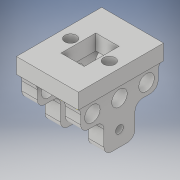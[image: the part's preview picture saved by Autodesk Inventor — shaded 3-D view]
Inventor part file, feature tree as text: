
AUTODESK INVENTOR PART (.ipt)
format: ipt  version: 2019 (Build 230136000, 136)  size: 258,048 bytes
history: native  units: mm
features: extrude x8, sketch x8, fillet x4, hole x1
ambient origin geometry x8: Origin, YZ Plane, XZ Plane, XY Plane, X Axis, Y Axis, Z Axis, Center Point
bodies: Solid1 (feature_tree)
feature tree (21):
  extrude  "Extrusion1"  Depth=80.0mm
  extrude  "Extrusion2"  Depth=30.0mm
  hole  "Hole1"  [1 undecoded]
  extrude  "Extrusion3"  Depth=20.0mm
  fillet  "Fillet1"  Radius=2.0mm
  fillet  "Fillet3"  Radius=30.0mm
  extrude  "Extrusion4"  Depth=15.0mm
  sketch  "Sketch6"  dims[d20=15.0mm d21=25.0mm]
  extrude  "Extrusion6"  Depth=25.0mm
  extrude  "Extrusion7"  Depth=15.0mm TaperAngle=0.0deg
  extrude  "Extrusion8"  Depth=10.0mm
  extrude  "Extrusion9"  Depth=45.0mm
  fillet  "Fillet7"  Radius=30.0mm
  fillet  "Fillet8"  Radius=20.0mm
  sketch  "Sketch1"  dims[d0=110.0mm d1=80.0mm]
  sketch  "Sketch2"  dims[d2=20.0mm d3=0.0mm d4=30.0mm]
  sketch  "Sketch3"  dims[d5=20.0mm d6=20.0mm]
  sketch  "Sketch4"  dims[d7=2.0mm d8=20.0mm d9=2.0mm d10=30.0mm d11=0.0mm]
  sketch  "Sketch5"  dims[d12=20.0mm d13=6.0mm d14=4.0mm d15=2.0mm d16=90.0deg d17=15.0mm d18=20.594885mm d19=15.0mm]
  sketch  "Sketch7"  dims[d23=25.0mm d24=15.0mm d25=0.0mm]
  sketch  "Sketch9"  dims[d26=10.0mm d28=10.0mm d30=45.0mm d31=30.0mm d32=20.0mm d33=0.0mm d37=70.0mm d38=0.0mm d39=70.0mm d40=0.0mm d42=20.0mm d43=15.0mm d44=100.0mm d45=0.0mm d46=10.0mm d47=20.0mm d48=100.0mm d49=0.0mm d50=10.0mm d51=10.0mm d22=0.75mm]
note: 1 required parameter value undecoded (feature->parameter linkage not recoverable at this tier; creation-order binding heuristic only, values carry confidence <= 0.55)
